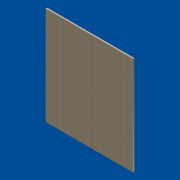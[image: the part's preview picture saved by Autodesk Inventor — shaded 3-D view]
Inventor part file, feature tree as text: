
AUTODESK INVENTOR PART (.ipt)
format: ipt  version: 2012 SP1 (Build 160190100, 190)  size: 76,800 bytes
history: native  units: in
note: dims shown in document units (in); Inventor stores cm internally (conversion verified against a paired STEP export)
features: extrude x1, sketch x1
ambient origin geometry x8: Origin, YZ Plane, XZ Plane, XY Plane, X Axis, Y Axis, Z Axis, Center Point
bodies: Solid1 (feature_tree)
feature tree (2):
  extrude  "Extrusion1"  Depth=17.7165in
  sketch  "Sketch1"  dims[d0=15.748in d1=17.7165in d2=7.874in d3=8.8583in d4=0.25in d5=0.0in]
